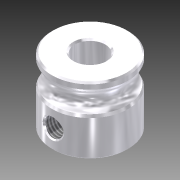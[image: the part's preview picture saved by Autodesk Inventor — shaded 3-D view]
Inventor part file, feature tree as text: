
AUTODESK INVENTOR PART (.ipt)
format: ipt  version: 2016 SP1 (Build 200210100, 210)  size: 176,640 bytes
history: native  units: mm
features: sketch x4, other x3
ambient origin geometry x8: Origin, YZ Plane, XZ Plane, XY Plane, X Axis, Y Axis, Z Axis, Center Point
bodies: Solid1 (feature_tree)
feature tree (7):
  other  "Drive Gear.ipt"
  other  "Solid1::Drive Gear.ipt"
  other  "TaggingFeature1"
  sketch  "Sketch1"  dims[d0=10.0mm]
  sketch  "Sketch2"
  sketch  "Sketch3"
  sketch  "Sketch4"
